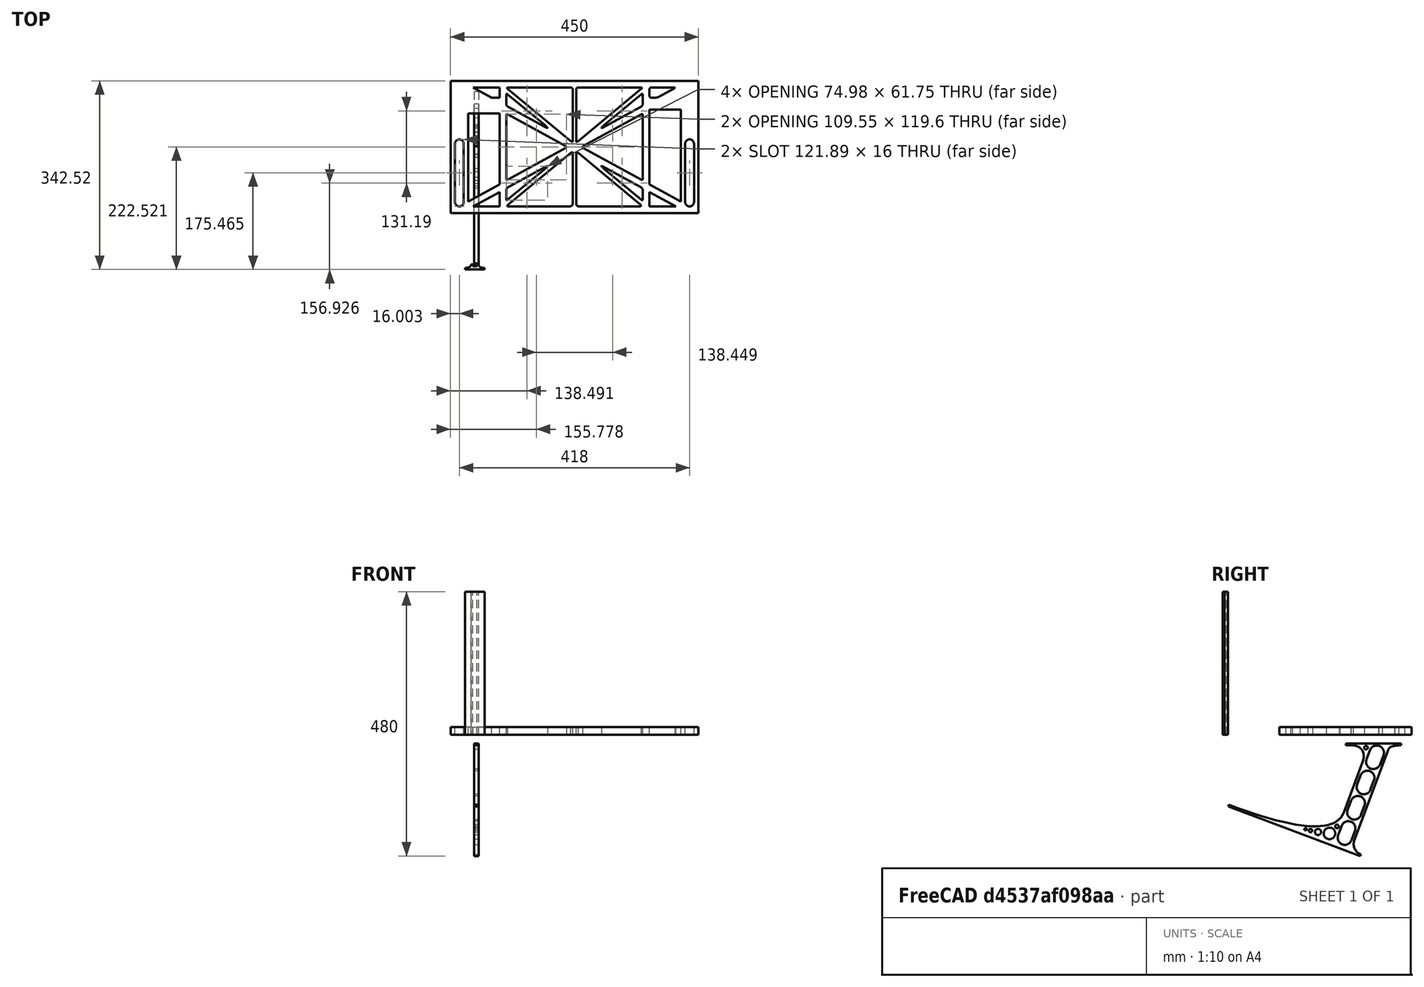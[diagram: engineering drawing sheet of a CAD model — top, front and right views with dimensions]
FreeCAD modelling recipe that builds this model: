
FCSTD DOCUMENT  (FreeCAD 0.19R0.19.2)
Label: laptopStand105
License: All rights reserved
LicenseURL: http://en.wikipedia.org/wiki/All_rights_reserved
objects: Sketcher::SketchObject×3, Part::Extrusion×3
note: 6 computed .brp shape members not serialized (recipe doc carries the construction recipe); baked Part::Feature solids carry a one-line shape summary decoded from their .brp

FEATURE [Sketcher::SketchObject] Sketch
  FullyConstrained = false
  sketch-geometry (288):
    g0: LineSegment StartX=-10.9272 StartY=-82.7794 StartZ=0 EndX=46.0728 EndY=-51.4823 EndZ=0
    g1: LineSegment StartX=366.073 StartY=-91.7794 StartZ=0 EndX=318.073 EndY=-65.424 EndZ=0
    g2: LineSegment StartX=-10.9272 StartY=77.3346 StartZ=0 EndX=-10.9272 EndY=-82.7794 EndZ=0
    g3: LineSegment StartX=-1.92719 StartY=-91.7794 StartZ=0 EndX=46.0728 EndY=-91.7794 EndZ=0
    g4: LineSegment StartX=318.073 StartY=-65.424 StartZ=0 EndX=318.073 EndY=-91.7794 EndZ=0
    g5: LineSegment StartX=318.073 StartY=-91.7794 StartZ=0 EndX=366.073 EndY=-91.7794 EndZ=0
    g6: LineSegment StartX=46.0728 StartY=-65.424 StartZ=0 EndX=-1.92719 EndY=-91.7794 EndZ=0
    g7: LineSegment StartX=46.0728 StartY=-65.424 StartZ=0 EndX=46.0728 EndY=-91.7794 EndZ=0
    g8: LineSegment StartX=46.0728 StartY=77.3346 StartZ=0 EndX=46.0728 EndY=-51.4823 EndZ=0
    g9: LineSegment StartX=-42.9272 StartY=136.221 StartZ=0 EndX=-42.9272 EndY=-103.779 EndZ=0
    g10: LineSegment StartX=407.073 StartY=136.221 StartZ=0 EndX=407.073 EndY=-103.779 EndZ=0
    g11: ArcOfCircle CenterX=-26.9272 CenterY=22.1087 CenterZ=0 NormalX=0 NormalY=0 NormalZ=1 AngleXU=0 Radius=8 StartAngle=1e-16 EndAngle=3.14159
    g12: ArcOfCircle CenterX=-26.9272 CenterY=-83.7794 CenterZ=0 NormalX=0 NormalY=0 NormalZ=1 AngleXU=0 Radius=8 StartAngle=3.14159 EndAngle=6.28319
    g13: LineSegment StartX=-34.9272 StartY=22.1087 StartZ=0 EndX=-34.9272 EndY=-83.7794 EndZ=0
    g14: LineSegment StartX=-18.9272 StartY=22.1087 StartZ=0 EndX=-18.9272 EndY=-83.7794 EndZ=0
    g15: ArcOfCircle CenterX=391.073 CenterY=22.1087 CenterZ=0 NormalX=0 NormalY=0 NormalZ=1 AngleXU=0 Radius=8 StartAngle=-4.4e-15 EndAngle=3.14159
    g16: LineSegment StartX=399.073 StartY=22.1087 StartZ=0 EndX=399.073 EndY=-83.7794 EndZ=0
    g17: LineSegment StartX=383.073 StartY=22.1087 StartZ=0 EndX=383.073 EndY=-83.7794 EndZ=0
    g18: ArcOfCircle CenterX=391.073 CenterY=-83.7794 CenterZ=0 NormalX=0 NormalY=0 NormalZ=1 AngleXU=0 Radius=8 StartAngle=3.14159 EndAngle=6.28319
    g19: Circle CenterX=175.022 CenterY=27.0628 CenterZ=0 NormalX=0 NormalY=0 NormalZ=1 AngleXU=0 Radius=1
    g20: Circle CenterX=179.022 CenterY=24.8665 CenterZ=0 NormalX=0 NormalY=0 NormalZ=1 AngleXU=0 Radius=1
    g21: Circle CenterX=179.022 CenterY=27.0628 CenterZ=0 NormalX=0 NormalY=0 NormalZ=1 AngleXU=0 Radius=1
    g22: BSplineCurve PolesCount=3 KnotsCount=2 Degree=2 IsPeriodic=0
    g23: GeomPoint X=175.022 Y=27.0628 Z=0
    g24: GeomPoint X=179.022 Y=27.0628 Z=0
    g25: Circle CenterX=189.124 CenterY=27.0628 CenterZ=0 NormalX=0 NormalY=0 NormalZ=1 AngleXU=0 Radius=1
    g26: Circle CenterX=185.124 CenterY=24.8665 CenterZ=0 NormalX=0 NormalY=0 NormalZ=1 AngleXU=0 Radius=1
    g27: Circle CenterX=185.124 CenterY=27.0628 CenterZ=0 NormalX=0 NormalY=0 NormalZ=1 AngleXU=0 Radius=1
    g28: BSplineCurve PolesCount=3 KnotsCount=2 Degree=2 IsPeriodic=0
    g29: GeomPoint X=189.124 Y=27.0628 Z=0
    g30: GeomPoint X=185.124 Y=27.0628 Z=0
    g31: Circle CenterX=175.022 CenterY=5.37834 CenterZ=0 NormalX=0 NormalY=0 NormalZ=1 AngleXU=0 Radius=1
    g32: Circle CenterX=179.022 CenterY=7.57463 CenterZ=0 NormalX=0 NormalY=0 NormalZ=1 AngleXU=0 Radius=1
    g33: Circle CenterX=179.022 CenterY=5.34704 CenterZ=0 NormalX=0 NormalY=0 NormalZ=1 AngleXU=0 Radius=1
    g34: BSplineCurve PolesCount=3 KnotsCount=2 Degree=2 IsPeriodic=0
    g35: GeomPoint X=175.022 Y=5.37834 Z=0
    g36: GeomPoint X=179.022 Y=5.34704 Z=0
    g37: Circle CenterX=189.124 CenterY=5.37834 CenterZ=0 NormalX=0 NormalY=0 NormalZ=1 AngleXU=0 Radius=1
    g38: Circle CenterX=185.124 CenterY=7.57463 CenterZ=0 NormalX=0 NormalY=0 NormalZ=1 AngleXU=0 Radius=1
    g39: Circle CenterX=185.124 CenterY=5.34704 CenterZ=0 NormalX=0 NormalY=0 NormalZ=1 AngleXU=0 Radius=1
    g40: BSplineCurve PolesCount=3 KnotsCount=2 Degree=2 IsPeriodic=0
    g41: GeomPoint X=189.124 Y=5.37834 Z=0
    g42: GeomPoint X=185.124 Y=5.34704 Z=0
    g43: Circle CenterX=165.871 CenterY=18.1458 CenterZ=0 NormalX=0 NormalY=0 NormalZ=1 AngleXU=0 Radius=1
    g44: Circle CenterX=169.377 CenterY=16.2206 CenterZ=0 NormalX=0 NormalY=0 NormalZ=1 AngleXU=0 Radius=1
    g45: Circle CenterX=165.871 CenterY=14.2954 CenterZ=0 NormalX=0 NormalY=0 NormalZ=1 AngleXU=0 Radius=1
    g46: BSplineCurve PolesCount=3 KnotsCount=2 Degree=2 IsPeriodic=0
    g47: GeomPoint X=165.871 Y=18.1458 Z=0
    g48: GeomPoint X=165.871 Y=14.2954 Z=0
    g49: Circle CenterX=198.275 CenterY=18.1458 CenterZ=0 NormalX=0 NormalY=0 NormalZ=1 AngleXU=0 Radius=1
    g50: Circle CenterX=194.768 CenterY=16.2206 CenterZ=0 NormalX=0 NormalY=0 NormalZ=1 AngleXU=0 Radius=1
    g51: Circle CenterX=198.275 CenterY=14.2954 CenterZ=0 NormalX=0 NormalY=0 NormalZ=1 AngleXU=0 Radius=1
    g52: BSplineCurve PolesCount=3 KnotsCount=2 Degree=2 IsPeriodic=0
    g53: GeomPoint X=198.275 Y=18.1458 Z=0
    g54: GeomPoint X=198.275 Y=14.2954 Z=0
    g55: LineSegment StartX=407.073 StartY=-103.779 StartZ=0 EndX=-42.9272 EndY=-103.779 EndZ=0
    g56: LineSegment StartX=407.073 StartY=136.221 StartZ=0 EndX=-42.9272 EndY=136.221 EndZ=0
    g57: LineSegment StartX=46.0728 StartY=77.3346 StartZ=0 EndX=-10.9272 EndY=77.3346 EndZ=0
    g58: LineSegment StartX=46.0728 StartY=105.865 StartZ=0 EndX=31.5028 EndY=105.865 EndZ=0
    g59: LineSegment StartX=46.0728 StartY=124.221 StartZ=0 EndX=46.0728 EndY=105.865 EndZ=0
    g60: LineSegment StartX=-1.92719 StartY=124.221 StartZ=0 EndX=31.5028 EndY=105.865 EndZ=0
    g61: LineSegment StartX=46.0728 StartY=124.221 StartZ=0 EndX=-1.92719 EndY=124.221 EndZ=0
    g62: Circle CenterX=125.607 CenterY=54.1951 CenterZ=0 NormalX=0 NormalY=0 NormalZ=1 AngleXU=0 Radius=1
    g63: Circle CenterX=139.632 CenterY=46.4944 CenterZ=0 NormalX=0 NormalY=0 NormalZ=1 AngleXU=0 Radius=1
    g64: Circle CenterX=127.326 CenterY=56.7187 CenterZ=0 NormalX=0 NormalY=0 NormalZ=1 AngleXU=0 Radius=1
    g65: BSplineCurve PolesCount=3 KnotsCount=2 Degree=2 IsPeriodic=0
    g66: GeomPoint X=125.607 Y=54.1951 Z=0
    g67: GeomPoint X=127.326 Y=56.7187 Z=0
    g68: Circle CenterX=236.821 CenterY=56.7187 CenterZ=0 NormalX=0 NormalY=0 NormalZ=1 AngleXU=0 Radius=1
    g69: Circle CenterX=224.513 CenterY=46.4944 CenterZ=0 NormalX=0 NormalY=0 NormalZ=1 AngleXU=0 Radius=1
    g70: Circle CenterX=238.538 CenterY=54.1951 CenterZ=0 NormalX=0 NormalY=0 NormalZ=1 AngleXU=0 Radius=1
    g71: BSplineCurve PolesCount=3 KnotsCount=2 Degree=2 IsPeriodic=0
    g72: GeomPoint X=236.821 Y=56.7187 Z=0
    g73: GeomPoint X=238.538 Y=54.1951 Z=0
    g74: Circle CenterX=238.538 CenterY=-21.7539 CenterZ=0 NormalX=0 NormalY=0 NormalZ=1 AngleXU=0 Radius=1
    g75: Circle CenterX=224.513 CenterY=-14.0532 CenterZ=0 NormalX=0 NormalY=0 NormalZ=1 AngleXU=0 Radius=1
    g76: Circle CenterX=236.821 CenterY=-24.2775 CenterZ=0 NormalX=0 NormalY=0 NormalZ=1 AngleXU=0 Radius=1
    g77: BSplineCurve PolesCount=3 KnotsCount=2 Degree=2 IsPeriodic=0
    g78: GeomPoint X=238.538 Y=-21.7539 Z=0
    g79: GeomPoint X=236.821 Y=-24.2775 Z=0
    g80: Circle CenterX=125.607 CenterY=-21.7539 CenterZ=0 NormalX=0 NormalY=0 NormalZ=1 AngleXU=0 Radius=1
    g81: Circle CenterX=139.632 CenterY=-14.0532 CenterZ=0 NormalX=0 NormalY=0 NormalZ=1 AngleXU=0 Radius=1
    g82: Circle CenterX=127.325 CenterY=-24.2775 CenterZ=0 NormalX=0 NormalY=0 NormalZ=1 AngleXU=0 Radius=1
    g83: BSplineCurve PolesCount=3 KnotsCount=2 Degree=2 IsPeriodic=0
    g84: GeomPoint X=125.607 Y=-21.7539 Z=0
    g85: GeomPoint X=127.325 Y=-24.2775 Z=0
    g86: Circle CenterX=302.996 CenterY=111.695 CenterZ=0 NormalX=0 NormalY=0 NormalZ=1 AngleXU=0 Radius=1
    g87: Circle CenterX=306.073 CenterY=114.251 CenterZ=0 NormalX=0 NormalY=0 NormalZ=1 AngleXU=0 Radius=1
    g88: Circle CenterX=306.073 CenterY=110.251 CenterZ=0 NormalX=0 NormalY=0 NormalZ=1 AngleXU=0 Radius=1
    g89: BSplineCurve PolesCount=3 KnotsCount=2 Degree=2 IsPeriodic=0
    g90: GeomPoint X=302.996 Y=111.695 Z=0
    g91: GeomPoint X=306.073 Y=110.251 Z=0
    g92: Circle CenterX=306.073 CenterY=95.2763 CenterZ=0 NormalX=0 NormalY=0 NormalZ=1 AngleXU=0 Radius=1
    g93: Circle CenterX=306.073 CenterY=91.2763 CenterZ=0 NormalX=0 NormalY=0 NormalZ=1 AngleXU=0 Radius=1
    g94: Circle CenterX=302.567 CenterY=89.3511 CenterZ=0 NormalX=0 NormalY=0 NormalZ=1 AngleXU=0 Radius=1
    g95: BSplineCurve PolesCount=3 KnotsCount=2 Degree=2 IsPeriodic=0
    g96: GeomPoint X=306.073 Y=95.2763 Z=0
    g97: GeomPoint X=302.567 Y=89.3511 Z=0
    g98: LineSegment StartX=306.073 StartY=110.251 StartZ=0 EndX=306.073 EndY=95.2763 EndZ=0
    g99: LineSegment StartX=302.996 StartY=111.695 StartZ=0 EndX=236.821 EndY=56.7187 EndZ=0
    g100: LineSegment StartX=238.538 StartY=54.1951 StartZ=0 EndX=302.567 EndY=89.3511 EndZ=0
    g101: Circle CenterX=61.1496 CenterY=111.695 CenterZ=0 NormalX=0 NormalY=0 NormalZ=1 AngleXU=0 Radius=1
    g102: Circle CenterX=58.0728 CenterY=114.251 CenterZ=0 NormalX=0 NormalY=0 NormalZ=1 AngleXU=0 Radius=1
    g103: Circle CenterX=58.0728 CenterY=110.251 CenterZ=0 NormalX=0 NormalY=0 NormalZ=1 AngleXU=0 Radius=1
    g104: BSplineCurve PolesCount=3 KnotsCount=2 Degree=2 IsPeriodic=0
    g105: GeomPoint X=61.1496 Y=111.695 Z=0
    g106: GeomPoint X=58.0728 Y=110.251 Z=0
    g107: Circle CenterX=61.5791 CenterY=89.3511 CenterZ=0 NormalX=0 NormalY=0 NormalZ=1 AngleXU=0 Radius=1
    g108: Circle CenterX=58.0728 CenterY=91.2763 CenterZ=0 NormalX=0 NormalY=0 NormalZ=1 AngleXU=0 Radius=1
    g109: Circle CenterX=58.0728 CenterY=95.2763 CenterZ=0 NormalX=0 NormalY=0 NormalZ=1 AngleXU=0 Radius=1
    g110: BSplineCurve PolesCount=3 KnotsCount=2 Degree=2 IsPeriodic=0
    g111: GeomPoint X=61.5791 Y=89.3511 Z=0
    g112: GeomPoint X=58.0728 Y=95.2763 Z=0
    g113: LineSegment StartX=58.0728 StartY=110.251 StartZ=0 EndX=58.0728 EndY=95.2763 EndZ=0
    g114: LineSegment StartX=61.1496 StartY=111.695 StartZ=0 EndX=127.326 EndY=56.7187 EndZ=0
    g115: LineSegment StartX=125.607 StartY=54.1951 StartZ=0 EndX=61.5791 EndY=89.3511 EndZ=0
    g116: Circle CenterX=61.5791 CenterY=-56.9099 CenterZ=0 NormalX=0 NormalY=0 NormalZ=1 AngleXU=0 Radius=1
    g117: Circle CenterX=58.0728 CenterY=-58.8351 CenterZ=0 NormalX=0 NormalY=0 NormalZ=1 AngleXU=0 Radius=1
    g118: Circle CenterX=58.0728 CenterY=-62.8351 CenterZ=0 NormalX=0 NormalY=0 NormalZ=1 AngleXU=0 Radius=1
    g119: BSplineCurve PolesCount=3 KnotsCount=2 Degree=2 IsPeriodic=0
    g120: GeomPoint X=61.5791 Y=-56.9099 Z=0
    g121: GeomPoint X=58.0728 Y=-62.8351 Z=0
    g122: Circle CenterX=58.0728 CenterY=-77.8102 CenterZ=0 NormalX=0 NormalY=0 NormalZ=1 AngleXU=0 Radius=1
    g123: Circle CenterX=58.0728 CenterY=-81.8102 CenterZ=0 NormalX=0 NormalY=0 NormalZ=1 AngleXU=0 Radius=1
    g124: Circle CenterX=61.1496 CenterY=-79.2541 CenterZ=0 NormalX=0 NormalY=0 NormalZ=1 AngleXU=0 Radius=1
    g125: BSplineCurve PolesCount=3 KnotsCount=2 Degree=2 IsPeriodic=0
    g126: GeomPoint X=58.0728 Y=-77.8102 Z=0
    g127: GeomPoint X=61.1496 Y=-79.2541 Z=0
    g128: LineSegment StartX=58.0728 StartY=-62.8351 StartZ=0 EndX=58.0728 EndY=-77.8102 EndZ=0
    g129: LineSegment StartX=61.1496 StartY=-79.2541 StartZ=0 EndX=127.325 EndY=-24.2775 EndZ=0
    g130: LineSegment StartX=125.607 StartY=-21.7539 StartZ=0 EndX=61.5791 EndY=-56.9099 EndZ=0
    g131: Circle CenterX=302.567 CenterY=-56.9099 CenterZ=0 NormalX=0 NormalY=0 NormalZ=1 AngleXU=0 Radius=1
    g132: Circle CenterX=306.073 CenterY=-58.8351 CenterZ=0 NormalX=0 NormalY=0 NormalZ=1 AngleXU=0 Radius=1
    g133: Circle CenterX=306.073 CenterY=-62.8351 CenterZ=0 NormalX=0 NormalY=0 NormalZ=1 AngleXU=0 Radius=1
    g134: BSplineCurve PolesCount=3 KnotsCount=2 Degree=2 IsPeriodic=0
    g135: GeomPoint X=302.567 Y=-56.9099 Z=0
    g136: GeomPoint X=306.073 Y=-62.8351 Z=0
    g137: Circle CenterX=302.996 CenterY=-79.2541 CenterZ=0 NormalX=0 NormalY=0 NormalZ=1 AngleXU=0 Radius=1
    g138: Circle CenterX=306.073 CenterY=-81.8102 CenterZ=0 NormalX=0 NormalY=0 NormalZ=1 AngleXU=0 Radius=1
    g139: Circle CenterX=306.073 CenterY=-77.8102 CenterZ=0 NormalX=0 NormalY=0 NormalZ=1 AngleXU=0 Radius=1
    g140: BSplineCurve PolesCount=3 KnotsCount=2 Degree=2 IsPeriodic=0
    g141: GeomPoint X=302.996 Y=-79.2541 Z=0
    g142: GeomPoint X=306.073 Y=-77.8102 Z=0
    g143: LineSegment StartX=306.073 StartY=-62.8351 StartZ=0 EndX=306.073 EndY=-77.8102 EndZ=0
    g144: LineSegment StartX=302.996 StartY=-79.2541 StartZ=0 EndX=236.821 EndY=-24.2775 EndZ=0
    g145: LineSegment StartX=238.538 StartY=-21.7539 StartZ=0 EndX=302.567 EndY=-56.9099 EndZ=0
    g146: Circle CenterX=61.6457 CenterY=-88.8112 CenterZ=0 NormalX=0 NormalY=0 NormalZ=1 AngleXU=0 Radius=1
    g147: Circle CenterX=58.0728 CenterY=-91.7794 CenterZ=0 NormalX=0 NormalY=0 NormalZ=1 AngleXU=0 Radius=1
    g148: Circle CenterX=63.9135 CenterY=-91.7794 CenterZ=0 NormalX=0 NormalY=0 NormalZ=1 AngleXU=0 Radius=1
    g149: BSplineCurve PolesCount=3 KnotsCount=2 Degree=2 IsPeriodic=0
    g150: GeomPoint X=61.6457 Y=-88.8112 Z=0
    g151: GeomPoint X=63.9135 Y=-91.7794 Z=0
    g152: Circle CenterX=179.022 CenterY=-85.8163 CenterZ=0 NormalX=0 NormalY=0 NormalZ=1 AngleXU=0 Radius=1
    g153: Circle CenterX=179.022 CenterY=-91.7794 CenterZ=0 NormalX=0 NormalY=0 NormalZ=1 AngleXU=0 Radius=1
    g154: Circle CenterX=171.895 CenterY=-91.7794 CenterZ=0 NormalX=0 NormalY=0 NormalZ=1 AngleXU=0 Radius=1
    g155: BSplineCurve PolesCount=3 KnotsCount=2 Degree=2 IsPeriodic=0
    g156: GeomPoint X=179.022 Y=-85.8163 Z=0
    g157: GeomPoint X=171.895 Y=-91.7794 Z=0
    g158: Circle CenterX=185.124 CenterY=-86.2028 CenterZ=0 NormalX=0 NormalY=0 NormalZ=1 AngleXU=0 Radius=1
    g159: Circle CenterX=185.124 CenterY=-91.7794 CenterZ=0 NormalX=0 NormalY=0 NormalZ=1 AngleXU=0 Radius=1
    g160: Circle CenterX=191.747 CenterY=-91.7794 CenterZ=0 NormalX=0 NormalY=0 NormalZ=1 AngleXU=0 Radius=1
    g161: BSplineCurve PolesCount=3 KnotsCount=2 Degree=2 IsPeriodic=0
    g162: GeomPoint X=185.124 Y=-86.2028 Z=0
    g163: GeomPoint X=191.747 Y=-91.7794 Z=0
    g164: Circle CenterX=299.888 CenterY=-86.6413 CenterZ=0 NormalX=0 NormalY=0 NormalZ=1 AngleXU=0 Radius=1
    g165: Circle CenterX=306.073 CenterY=-91.7794 CenterZ=0 NormalX=0 NormalY=0 NormalZ=1 AngleXU=0 Radius=1
    g166: Circle CenterX=298.776 CenterY=-91.7794 CenterZ=0 NormalX=0 NormalY=0 NormalZ=1 AngleXU=0 Radius=1
    g167: BSplineCurve PolesCount=3 KnotsCount=2 Degree=2 IsPeriodic=0
    g168: GeomPoint X=299.888 Y=-86.6413 Z=0
    g169: GeomPoint X=298.776 Y=-91.7794 Z=0
    g170: LineSegment StartX=189.124 StartY=5.37834 StartZ=0 EndX=299.888 EndY=-86.6413 EndZ=0
    g171: LineSegment StartX=298.776 StartY=-91.7794 StartZ=0 EndX=191.747 EndY=-91.7794 EndZ=0
    g172: LineSegment StartX=185.124 StartY=-86.2028 StartZ=0 EndX=185.124 EndY=5.34704 EndZ=0
    g173: LineSegment StartX=179.022 StartY=5.34704 StartZ=0 EndX=179.022 EndY=-85.8163 EndZ=0
    g174: LineSegment StartX=171.895 StartY=-91.7794 StartZ=0 EndX=63.9135 EndY=-91.7794 EndZ=0
    g175: LineSegment StartX=61.6457 StartY=-88.8112 StartZ=0 EndX=175.022 EndY=5.37834 EndZ=0
    g176: Circle CenterX=302.073 CenterY=124.221 CenterZ=0 NormalX=0 NormalY=0 NormalZ=1 AngleXU=0 Radius=1
    g177: Circle CenterX=306.073 CenterY=124.221 CenterZ=0 NormalX=0 NormalY=0 NormalZ=1 AngleXU=0 Radius=1
    g178: Circle CenterX=302.996 CenterY=121.665 CenterZ=0 NormalX=0 NormalY=0 NormalZ=1 AngleXU=0 Radius=1
    g179: BSplineCurve PolesCount=3 KnotsCount=2 Degree=2 IsPeriodic=0
    g180: GeomPoint X=302.073 Y=124.221 Z=0
    g181: GeomPoint X=302.996 Y=121.665 Z=0
    g182: Circle CenterX=189.124 CenterY=124.221 CenterZ=0 NormalX=0 NormalY=0 NormalZ=1 AngleXU=0 Radius=1
    g183: Circle CenterX=185.124 CenterY=124.221 CenterZ=0 NormalX=0 NormalY=0 NormalZ=1 AngleXU=0 Radius=1
    g184: Circle CenterX=185.124 CenterY=120.221 CenterZ=0 NormalX=0 NormalY=0 NormalZ=1 AngleXU=0 Radius=1
    g185: BSplineCurve PolesCount=3 KnotsCount=2 Degree=2 IsPeriodic=0
    g186: GeomPoint X=189.124 Y=124.221 Z=0
    g187: GeomPoint X=185.124 Y=120.221 Z=0
    g188: Circle CenterX=175.022 CenterY=124.221 CenterZ=0 NormalX=0 NormalY=0 NormalZ=1 AngleXU=0 Radius=1
    g189: Circle CenterX=179.022 CenterY=124.221 CenterZ=0 NormalX=0 NormalY=0 NormalZ=1 AngleXU=0 Radius=1
    g190: Circle CenterX=179.022 CenterY=120.221 CenterZ=0 NormalX=0 NormalY=0 NormalZ=1 AngleXU=0 Radius=1
    g191: BSplineCurve PolesCount=3 KnotsCount=2 Degree=2 IsPeriodic=0
    g192: GeomPoint X=175.022 Y=124.221 Z=0
    g193: GeomPoint X=179.022 Y=120.221 Z=0
    g194: Circle CenterX=62.0728 CenterY=124.221 CenterZ=0 NormalX=0 NormalY=0 NormalZ=1 AngleXU=0 Radius=1
    g195: Circle CenterX=58.0728 CenterY=124.221 CenterZ=0 NormalX=0 NormalY=0 NormalZ=1 AngleXU=0 Radius=1
    g196: Circle CenterX=61.1496 CenterY=121.665 CenterZ=0 NormalX=0 NormalY=0 NormalZ=1 AngleXU=0 Radius=1
    g197: BSplineCurve PolesCount=3 KnotsCount=2 Degree=2 IsPeriodic=0
    g198: GeomPoint X=62.0728 Y=124.221 Z=0
    g199: GeomPoint X=61.1496 Y=121.665 Z=0
    g200: LineSegment StartX=62.0728 StartY=124.221 StartZ=0 EndX=175.022 EndY=124.221 EndZ=0
    g201: LineSegment StartX=179.022 StartY=120.221 StartZ=0 EndX=179.022 EndY=27.0628 EndZ=0
    g202: LineSegment StartX=185.124 StartY=27.0628 StartZ=0 EndX=185.124 EndY=120.221 EndZ=0
    g203: LineSegment StartX=189.124 StartY=124.221 StartZ=0 EndX=302.073 EndY=124.221 EndZ=0
    g204: LineSegment StartX=302.996 StartY=121.665 StartZ=0 EndX=189.124 EndY=27.0628 EndZ=0
    g205: LineSegment StartX=175.022 StartY=27.0628 StartZ=0 EndX=61.1496 EndY=121.665 EndZ=0
    g206: Circle CenterX=61.5791 CenterY=75.4095 CenterZ=0 NormalX=0 NormalY=0 NormalZ=1 AngleXU=0 Radius=1
    g207: Circle CenterX=58.0728 CenterY=77.3346 CenterZ=0 NormalX=0 NormalY=0 NormalZ=1 AngleXU=0 Radius=1
    g208: Circle CenterX=58.0728 CenterY=73.3346 CenterZ=0 NormalX=0 NormalY=0 NormalZ=1 AngleXU=0 Radius=1
    g209: BSplineCurve PolesCount=3 KnotsCount=2 Degree=2 IsPeriodic=0
    g210: GeomPoint X=61.5791 Y=75.4095 Z=0
    g211: GeomPoint X=58.0728 Y=73.3346 Z=0
    g212: Circle CenterX=58.0728 CenterY=-40.8935 CenterZ=0 NormalX=0 NormalY=0 NormalZ=1 AngleXU=0 Radius=1
    g213: Circle CenterX=58.0728 CenterY=-44.8935 CenterZ=0 NormalX=0 NormalY=0 NormalZ=1 AngleXU=0 Radius=1
    g214: Circle CenterX=61.5791 CenterY=-42.9683 CenterZ=0 NormalX=0 NormalY=0 NormalZ=1 AngleXU=0 Radius=1
    g215: BSplineCurve PolesCount=3 KnotsCount=2 Degree=2 IsPeriodic=0
    g216: GeomPoint X=58.0728 Y=-40.8935 Z=0
    g217: GeomPoint X=61.5791 Y=-42.9683 Z=0
    g218: LineSegment StartX=61.5791 StartY=-42.9683 StartZ=0 EndX=165.871 EndY=14.2954 EndZ=0
    g219: LineSegment StartX=165.871 StartY=18.1458 StartZ=0 EndX=61.5791 EndY=75.4095 EndZ=0
    g220: LineSegment StartX=58.0728 StartY=73.3346 StartZ=0 EndX=58.0728 EndY=-40.8935 EndZ=0
    g221: Circle CenterX=302.567 CenterY=-42.9683 CenterZ=0 NormalX=0 NormalY=0 NormalZ=1 AngleXU=0 Radius=1
    g222: Circle CenterX=306.073 CenterY=-44.8935 CenterZ=0 NormalX=0 NormalY=0 NormalZ=1 AngleXU=0 Radius=1
    g223: Circle CenterX=306.073 CenterY=-40.8935 CenterZ=0 NormalX=0 NormalY=0 NormalZ=1 AngleXU=0 Radius=1
    g224: BSplineCurve PolesCount=3 KnotsCount=2 Degree=2 IsPeriodic=0
    g225: GeomPoint X=302.567 Y=-42.9683 Z=0
    g226: GeomPoint X=306.073 Y=-40.8935 Z=0
    g227: Circle CenterX=306.073 CenterY=73.3346 CenterZ=0 NormalX=0 NormalY=0 NormalZ=1 AngleXU=0 Radius=1
    g228: Circle CenterX=306.073 CenterY=77.3346 CenterZ=0 NormalX=0 NormalY=0 NormalZ=1 AngleXU=0 Radius=1
    g229: Circle CenterX=302.567 CenterY=75.4095 CenterZ=0 NormalX=0 NormalY=0 NormalZ=1 AngleXU=0 Radius=1
    g230: BSplineCurve PolesCount=3 KnotsCount=2 Degree=2 IsPeriodic=0
    g231: GeomPoint X=306.073 Y=73.3346 Z=0
    g232: GeomPoint X=302.567 Y=75.4095 Z=0
    g233: LineSegment StartX=302.567 StartY=-42.9683 StartZ=0 EndX=198.275 EndY=14.2954 EndZ=0
    g234: LineSegment StartX=198.275 StartY=18.1458 StartZ=0 EndX=302.567 EndY=75.4095 EndZ=0
    g235: LineSegment StartX=306.073 StartY=73.3346 StartZ=0 EndX=306.073 EndY=-40.8935 EndZ=0
    g236: LineSegment StartX=322.073 StartY=105.865 StartZ=0 EndX=328.643 EndY=105.865 EndZ=0
    g237: LineSegment StartX=318.073 StartY=120.221 StartZ=0 EndX=318.073 EndY=109.865 EndZ=0
    g238: LineSegment StartX=336.157 StartY=107.779 StartZ=0 EndX=362.567 EndY=122.294 EndZ=0
    g239: Circle CenterX=362.073 CenterY=124.221 CenterZ=0 NormalX=0 NormalY=0 NormalZ=1 AngleXU=0 Radius=1
    g240: Circle CenterX=366.073 CenterY=124.221 CenterZ=0 NormalX=0 NormalY=0 NormalZ=1 AngleXU=0 Radius=1
    g241: Circle CenterX=362.567 CenterY=122.294 CenterZ=0 NormalX=0 NormalY=0 NormalZ=1 AngleXU=0 Radius=1
    g242: BSplineCurve PolesCount=3 KnotsCount=2 Degree=2 IsPeriodic=0
    g243: GeomPoint X=362.073 Y=124.221 Z=0
    g244: GeomPoint X=362.567 Y=122.294 Z=0
    g245: Circle CenterX=322.073 CenterY=124.221 CenterZ=0 NormalX=0 NormalY=0 NormalZ=1 AngleXU=0 Radius=1
    g246: Circle CenterX=318.073 CenterY=124.221 CenterZ=0 NormalX=0 NormalY=0 NormalZ=1 AngleXU=0 Radius=1
    g247: Circle CenterX=318.073 CenterY=120.221 CenterZ=0 NormalX=0 NormalY=0 NormalZ=1 AngleXU=0 Radius=1
    g248: BSplineCurve PolesCount=3 KnotsCount=2 Degree=2 IsPeriodic=0
    g249: GeomPoint X=322.073 Y=124.221 Z=0
    g250: GeomPoint X=318.073 Y=120.221 Z=0
    g251: Circle CenterX=322.073 CenterY=105.865 CenterZ=0 NormalX=0 NormalY=0 NormalZ=1 AngleXU=0 Radius=1
    g252: Circle CenterX=318.073 CenterY=105.865 CenterZ=0 NormalX=0 NormalY=0 NormalZ=1 AngleXU=0 Radius=1
    g253: Circle CenterX=318.073 CenterY=109.865 CenterZ=0 NormalX=0 NormalY=0 NormalZ=1 AngleXU=0 Radius=1
    g254: BSplineCurve PolesCount=3 KnotsCount=2 Degree=2 IsPeriodic=0
    g255: GeomPoint X=322.073 Y=105.865 Z=0
    g256: GeomPoint X=318.073 Y=109.865 Z=0
    g257: Circle CenterX=336.157 CenterY=107.779 CenterZ=0 NormalX=0 NormalY=0 NormalZ=1 AngleXU=0 Radius=1
    g258: Circle CenterX=332.651 CenterY=105.853 CenterZ=0 NormalX=0 NormalY=0 NormalZ=1 AngleXU=0 Radius=1
    g259: Circle CenterX=328.643 CenterY=105.865 CenterZ=0 NormalX=0 NormalY=0 NormalZ=1 AngleXU=0 Radius=1
    g260: BSplineCurve PolesCount=3 KnotsCount=2 Degree=2 IsPeriodic=0
    g261: GeomPoint X=336.157 Y=107.779 Z=0
    g262: GeomPoint X=328.643 Y=105.865 Z=0
    g263: LineSegment StartX=322.073 StartY=124.221 StartZ=0 EndX=362.073 EndY=124.221 EndZ=0
    g264: Circle CenterX=371.567 CenterY=-80.8644 CenterZ=0 NormalX=0 NormalY=0 NormalZ=1 AngleXU=0 Radius=1
    g265: Circle CenterX=375.073 CenterY=-82.7896 CenterZ=0 NormalX=0 NormalY=0 NormalZ=1 AngleXU=0 Radius=1
    g266: Circle CenterX=375.073 CenterY=-78.7896 CenterZ=0 NormalX=0 NormalY=0 NormalZ=1 AngleXU=0 Radius=1
    g267: BSplineCurve PolesCount=3 KnotsCount=2 Degree=2 IsPeriodic=0
    g268: GeomPoint X=371.567 Y=-80.8644 Z=0
    g269: GeomPoint X=375.073 Y=-78.7896 Z=0
    g270: Circle CenterX=321.579 CenterY=-53.4075 CenterZ=0 NormalX=0 NormalY=0 NormalZ=1 AngleXU=0 Radius=1
    g271: Circle CenterX=318.073 CenterY=-51.4823 CenterZ=0 NormalX=0 NormalY=0 NormalZ=1 AngleXU=0 Radius=1
    g272: Circle CenterX=318.073 CenterY=-47.4823 CenterZ=0 NormalX=0 NormalY=0 NormalZ=1 AngleXU=0 Radius=1
    g273: BSplineCurve PolesCount=3 KnotsCount=2 Degree=2 IsPeriodic=0
    g274: GeomPoint X=321.579 Y=-53.4075 Z=0
    g275: GeomPoint X=318.073 Y=-47.4823 Z=0
    g276: Circle CenterX=318.073 CenterY=79.9235 CenterZ=0 NormalX=0 NormalY=0 NormalZ=1 AngleXU=0 Radius=1
    g277: Circle CenterX=318.073 CenterY=83.9235 CenterZ=0 NormalX=0 NormalY=0 NormalZ=1 AngleXU=0 Radius=1
    g278: Circle CenterX=322.073 CenterY=83.9235 CenterZ=0 NormalX=0 NormalY=0 NormalZ=1 AngleXU=0 Radius=1
    g279: BSplineCurve PolesCount=3 KnotsCount=2 Degree=2 IsPeriodic=0
    g280: GeomPoint X=318.073 Y=79.9235 Z=0
    g281: GeomPoint X=322.073 Y=83.9235 Z=0
    g282: Circle CenterX=375.073 CenterY=79.9235 CenterZ=0 NormalX=0 NormalY=0 NormalZ=1 AngleXU=0 Radius=1
    g283: Circle CenterX=375.073 CenterY=83.9235 CenterZ=0 NormalX=0 NormalY=0 NormalZ=1 AngleXU=0 Radius=1
    g284: Circle CenterX=371.073 CenterY=83.9235 CenterZ=0 NormalX=0 NormalY=0 NormalZ=1 AngleXU=0 Radius=1
    g285: BSplineCurve PolesCount=3 KnotsCount=2 Degree=2 IsPeriodic=0
    g286: GeomPoint X=375.073 Y=79.9235 Z=0
    g287: GeomPoint X=371.073 Y=83.9235 Z=0
  constraints (473):
    c: Horizontal(g3)
    c: Coincident(g4,g1)
    c: Coincident(g7,g6)
    c: Coincident(g0,g8)
    c: Block(g1)
    c: Block(g4)
    c: Block(g7)
    c: Block(g6)
    c: Block(g0)
    c: Block(g2)
    c: Block(g5)
    c: Block(g3)
    c: Vertical(g9)
    c: Vertical(g10)
    c: Block(g10)
    c: Block(g9)
    c: Tangent(g11,g14) = 1.5708
    c: Tangent(g11,g13) = -1.5708
    c: Tangent(g13,g12) = -1.5708
    c: Tangent(g14,g12) = 1.5708
    c: Vertical(g13)
    c: Equal(g11,g12)
    c: Block(g14)
    c: Block(g13)
    c: Tangent(g15,g16) = 1.5708
    c: Tangent(g16,g18) = 1.5708
    c: Equal(g15,g18)
    c: Coincident(g17,g15)
    c: Coincident(g17,g18)
    c: Block(g16)
    c: Block(g17)
    c: Weight(g19) = 1
    c: Equal(g19,g20)
    c: Equal(g19,g21)
    c: InternalAlignment(g19,g22)
    c: InternalAlignment(g20,g22)
    c: InternalAlignment(g21,g22)
    c: InternalAlignment(g23,g22)
    c: InternalAlignment(g24,g22)
    c: Weight(g25) = 1
    c: Equal(g25,g26)
    c: Equal(g25,g27)
    c: InternalAlignment(g25,g28)
    c: InternalAlignment(g26,g28)
    c: InternalAlignment(g27,g28)
    c: InternalAlignment(g29,g28)
    c: InternalAlignment(g30,g28)
    c: Block(g28)
    c: Block(g22)
    c: Weight(g31) = 1
    c: Equal(g31,g32)
    c: Equal(g31,g33)
    c: InternalAlignment(g31,g34)
    c: InternalAlignment(g32,g34)
    c: InternalAlignment(g33,g34)
    c: InternalAlignment(g35,g34)
    c: InternalAlignment(g36,g34)
    c: Weight(g37) = 1
    c: Equal(g37,g38)
    c: Equal(g37,g39)
    c: InternalAlignment(g37,g40)
    c: InternalAlignment(g38,g40)
    c: InternalAlignment(g39,g40)
    c: InternalAlignment(g41,g40)
    c: InternalAlignment(g42,g40)
    c: Block(g40)
    c: Block(g34)
    c: Weight(g43) = 1
    c: Equal(g43,g44)
    c: Equal(g43,g45)
    c: InternalAlignment(g43,g46)
    c: InternalAlignment(g44,g46)
    c: InternalAlignment(g45,g46)
    c: InternalAlignment(g47,g46)
    c: InternalAlignment(g48,g46)
    c: Weight(g49) = 1
    c: Equal(g49,g50)
    c: Equal(g49,g51)
    c: InternalAlignment(g49,g52)
    c: InternalAlignment(g50,g52)
    c: InternalAlignment(g51,g52)
    c: InternalAlignment(g53,g52)
    c: InternalAlignment(g54,g52)
    c: Block(g46)
    c: Block(g52)
    c: Coincident(g55,g10)
    c: Coincident(g55,g9)
    c: Horizontal(g55)
    c: Distance(g55) = 450
    c: Coincident(g56,g10)
    c: Coincident(g56,g9)
    c: Horizontal(g56)
    c: Horizontal(g57)
    c: Coincident(g8,g57)
    c: Horizontal(g58)
    c: Vertical(g59)
    c: Block(g59)
    c: Block(g58)
    c: Block(g57)
    c: Distance(g59) = 18.3554
    c: Coincident(g61,g59)
    c: Coincident(g61,g60)
    c: Horizontal(g61)
    c: Block(g61)
    c: Block(g60)
    c: Coincident(g58,g60)
    c: Coincident(g2,g57)
    c: Weight(g62) = 1
    c: Equal(g62,g63)
    c: Equal(g62,g64)
    c: InternalAlignment(g62,g65)
    c: InternalAlignment(g63,g65)
    c: InternalAlignment(g64,g65)
    c: InternalAlignment(g66,g65)
    c: InternalAlignment(g67,g65)
    c: Block(g65)
    c: Weight(g68) = 1
    c: Equal(g68,g69)
    c: Equal(g68,g70)
    c: InternalAlignment(g68,g71)
    c: InternalAlignment(g69,g71)
    c: InternalAlignment(g70,g71)
    c: InternalAlignment(g72,g71)
    c: InternalAlignment(g73,g71)
    c: Block(g71)
    c: Weight(g74) = 1
    c: Equal(g74,g75)
    c: Equal(g74,g76)
    c: InternalAlignment(g74,g77)
    c: InternalAlignment(g75,g77)
    c: InternalAlignment(g76,g77)
    c: InternalAlignment(g78,g77)
    c: InternalAlignment(g79,g77)
    c: Block(g77)
    c: Weight(g80) = 1
    c: Equal(g80,g81)
    c: Equal(g80,g82)
    c: InternalAlignment(g80,g83)
    c: InternalAlignment(g81,g83)
    c: InternalAlignment(g82,g83)
    c: InternalAlignment(g84,g83)
    c: InternalAlignment(g85,g83)
    c: Block(g83)
    c: Weight(g86) = 1
    c: Equal(g86,g87)
    c: Equal(g86,g88)
    c: InternalAlignment(g86,g89)
    c: InternalAlignment(g87,g89)
    c: InternalAlignment(g88,g89)
    c: InternalAlignment(g90,g89)
    c: InternalAlignment(g91,g89)
    c: Weight(g92) = 1
    c: Equal(g92,g93)
    c: Equal(g92,g94)
    c: InternalAlignment(g92,g95)
    c: InternalAlignment(g93,g95)
    c: InternalAlignment(g94,g95)
    c: InternalAlignment(g96,g95)
    c: InternalAlignment(g97,g95)
    c: Block(g89)
    c: Block(g95)
    c: Coincident(g98,g89)
    c: Coincident(g98,g95)
    c: Vertical(g98)
    c: Coincident(g99,g89)
    c: Coincident(g99,g71)
    c: Coincident(g100,g71)
    c: Coincident(g100,g95)
    c: Weight(g101) = 1
    c: Equal(g101,g102)
    c: Equal(g101,g103)
    c: InternalAlignment(g101,g104)
    c: InternalAlignment(g102,g104)
    c: InternalAlignment(g103,g104)
    c: InternalAlignment(g105,g104)
    c: InternalAlignment(g106,g104)
    c: Weight(g107) = 1
    c: Equal(g107,g108)
    c: Equal(g107,g109)
    c: InternalAlignment(g107,g110)
    c: InternalAlignment(g108,g110)
    c: InternalAlignment(g109,g110)
    c: InternalAlignment(g111,g110)
    c: InternalAlignment(g112,g110)
    c: Block(g104)
    c: Block(g110)
    c: Coincident(g113,g104)
    c: Coincident(g113,g110)
    c: Vertical(g113)
    c: Coincident(g114,g104)
    c: Coincident(g114,g65)
    c: Coincident(g115,g65)
    c: Coincident(g115,g110)
    c: Weight(g116) = 1
    c: Equal(g116,g117)
    c: Equal(g116,g118)
    c: InternalAlignment(g116,g119)
    c: InternalAlignment(g117,g119)
    c: InternalAlignment(g118,g119)
    c: InternalAlignment(g120,g119)
    c: InternalAlignment(g121,g119)
    c: Weight(g122) = 1
    c: Equal(g122,g123)
    c: Equal(g122,g124)
    c: InternalAlignment(g122,g125)
    c: InternalAlignment(g123,g125)
    c: InternalAlignment(g124,g125)
    c: InternalAlignment(g126,g125)
    c: InternalAlignment(g127,g125)
    c: Block(g119)
    c: Block(g125)
    c: Coincident(g128,g119)
    c: Coincident(g128,g125)
    c: Vertical(g128)
    c: Coincident(g129,g125)
    c: Coincident(g129,g83)
    c: Coincident(g130,g83)
    c: Coincident(g130,g119)
    c: Weight(g131) = 1
    c: Equal(g131,g132)
    c: Equal(g131,g133)
    c: InternalAlignment(g131,g134)
    c: InternalAlignment(g132,g134)
    c: InternalAlignment(g133,g134)
    c: InternalAlignment(g135,g134)
    c: InternalAlignment(g136,g134)
    c: Weight(g137) = 1
    c: Equal(g137,g138)
    c: Equal(g137,g139)
    c: InternalAlignment(g137,g140)
    c: InternalAlignment(g138,g140)
    c: InternalAlignment(g139,g140)
    c: InternalAlignment(g141,g140)
    c: InternalAlignment(g142,g140)
    c: Block(g134)
    c: Block(g140)
    c: Coincident(g143,g134)
    c: Coincident(g143,g140)
    c: Vertical(g143)
    c: Coincident(g144,g140)
    c: Coincident(g144,g77)
    c: Coincident(g145,g77)
    c: Coincident(g145,g134)
    c: Weight(g146) = 1
    c: Equal(g146,g147)
    c: Equal(g146,g148)
    c: InternalAlignment(g146,g149)
    c: InternalAlignment(g147,g149)
    c: InternalAlignment(g148,g149)
    c: InternalAlignment(g150,g149)
    c: InternalAlignment(g151,g149)
    c: Weight(g152) = 1
    c: Equal(g152,g153)
    c: Equal(g152,g154)
    c: InternalAlignment(g152,g155)
    c: InternalAlignment(g153,g155)
    c: InternalAlignment(g154,g155)
    c: InternalAlignment(g156,g155)
    c: InternalAlignment(g157,g155)
    c: Weight(g158) = 1
    c: Equal(g158,g159)
    c: Equal(g158,g160)
    c: InternalAlignment(g158,g161)
    c: InternalAlignment(g159,g161)
    c: InternalAlignment(g160,g161)
    c: InternalAlignment(g162,g161)
    c: InternalAlignment(g163,g161)
    c: Weight(g164) = 1
    c: Equal(g164,g165)
    c: Equal(g164,g166)
    c: InternalAlignment(g164,g167)
    c: InternalAlignment(g165,g167)
    c: InternalAlignment(g166,g167)
    c: InternalAlignment(g168,g167)
    c: InternalAlignment(g169,g167)
    c: Block(g167)
    c: Block(g161)
    c: Block(g155)
    c: Block(g149)
    c: Coincident(g170,g40)
    c: Coincident(g170,g167)
    c: Coincident(g171,g167)
    c: Coincident(g171,g161)
    c: Horizontal(g171)
    c: Coincident(g172,g161)
    c: Coincident(g172,g40)
    c: Vertical(g172)
    c: Coincident(g173,g34)
    c: Coincident(g173,g155)
    c: Vertical(g173)
    c: Coincident(g174,g155)
    c: Coincident(g174,g149)
    c: Horizontal(g174)
    c: Coincident(g175,g149)
    c: Coincident(g175,g34)
    c: Weight(g176) = 1
    c: Equal(g176,g177)
    c: Equal(g176,g178)
    c: InternalAlignment(g176,g179)
    c: InternalAlignment(g177,g179)
    c: InternalAlignment(g178,g179)
    c: InternalAlignment(g180,g179)
    c: InternalAlignment(g181,g179)
    c: Weight(g182) = 1
    c: Equal(g182,g183)
    c: Equal(g182,g184)
    c: InternalAlignment(g182,g185)
    c: InternalAlignment(g183,g185)
    c: InternalAlignment(g184,g185)
    c: InternalAlignment(g186,g185)
    c: InternalAlignment(g187,g185)
    c: Weight(g188) = 1
    c: Equal(g188,g189)
    c: Equal(g188,g190)
    c: InternalAlignment(g188,g191)
    c: InternalAlignment(g189,g191)
    c: InternalAlignment(g190,g191)
    c: InternalAlignment(g192,g191)
    c: InternalAlignment(g193,g191)
    c: Weight(g194) = 1
    c: Equal(g194,g195)
    c: Equal(g194,g196)
    c: InternalAlignment(g194,g197)
    c: InternalAlignment(g195,g197)
    c: InternalAlignment(g196,g197)
    c: InternalAlignment(g198,g197)
    c: InternalAlignment(g199,g197)
    c: Block(g197)
    c: Block(g191)
    c: Block(g185)
    c: Block(g179)
    c: Coincident(g200,g197)
    c: Coincident(g200,g191)
    c: Horizontal(g200)
    c: Coincident(g201,g191)
    c: Coincident(g201,g22)
    c: Vertical(g201)
    c: Coincident(g202,g28)
    c: Coincident(g202,g185)
    c: Vertical(g202)
    c: Coincident(g203,g185)
    c: Coincident(g203,g179)
    c: Horizontal(g203)
    c: Coincident(g204,g179)
    c: Coincident(g204,g28)
    c: Coincident(g205,g22)
    c: Weight(g206) = 1
    c: Equal(g206,g207)
    c: Equal(g206,g208)
    c: InternalAlignment(g206,g209)
    c: InternalAlignment(g207,g209)
    c: InternalAlignment(g208,g209)
    c: InternalAlignment(g210,g209)
    c: InternalAlignment(g211,g209)
    c: Weight(g212) = 1
    c: Equal(g212,g213)
    c: Equal(g212,g214)
    c: InternalAlignment(g212,g215)
    c: InternalAlignment(g213,g215)
    c: InternalAlignment(g214,g215)
    c: InternalAlignment(g216,g215)
    c: InternalAlignment(g217,g215)
    c: Block(g215)
    c: Block(g209)
    c: Coincident(g218,g215)
    c: Coincident(g218,g46)
    c: Coincident(g219,g46)
    c: Coincident(g219,g209)
    c: Coincident(g220,g209)
    c: Coincident(g220,g215)
    c: Vertical(g220)
    c: Weight(g221) = 1
    c: Equal(g221,g222)
    c: Equal(g221,g223)
    c: InternalAlignment(g221,g224)
    c: InternalAlignment(g222,g224)
    c: InternalAlignment(g223,g224)
    c: InternalAlignment(g225,g224)
    c: InternalAlignment(g226,g224)
    c: Weight(g227) = 1
    c: Equal(g227,g228)
    c: Equal(g227,g229)
    c: InternalAlignment(g227,g230)
    c: InternalAlignment(g228,g230)
    c: InternalAlignment(g229,g230)
    c: InternalAlignment(g231,g230)
    c: InternalAlignment(g232,g230)
    c: Block(g230)
    c: Block(g224)
    c: Coincident(g233,g224)
    c: Coincident(g233,g52)
    c: Coincident(g234,g52)
    c: Coincident(g234,g230)
    c: Coincident(g235,g230)
    c: Coincident(g235,g224)
    c: Vertical(g235)
    c: Horizontal(g236)
    c: Block(g236)
    c: Vertical(g237)
    c: Block(g237)
    c: Block(g238)
    c: Weight(g239) = 1
    c: Equal(g239,g240)
    c: Equal(g239,g241)
    c: InternalAlignment(g239,g242)
    c: InternalAlignment(g240,g242)
    c: InternalAlignment(g241,g242)
    c: InternalAlignment(g243,g242)
    c: InternalAlignment(g244,g242)
    c: Weight(g245) = 1
    c: Equal(g245,g246)
    c: Equal(g245,g247)
    c: InternalAlignment(g245,g248)
    c: InternalAlignment(g246,g248)
    c: InternalAlignment(g247,g248)
    c: InternalAlignment(g249,g248)
    c: InternalAlignment(g250,g248)
    c: Weight(g251) = 1
    c: Equal(g251,g252)
    c: Equal(g251,g253)
    c: InternalAlignment(g251,g254)
    c: InternalAlignment(g252,g254)
    c: InternalAlignment(g253,g254)
    c: InternalAlignment(g255,g254)
    c: InternalAlignment(g256,g254)
    c: Weight(g257) = 1
    c: Equal(g257,g258)
    c: Equal(g257,g259)
    c: InternalAlignment(g257,g260)
    c: InternalAlignment(g258,g260)
    c: InternalAlignment(g259,g260)
    c: InternalAlignment(g261,g260)
    c: InternalAlignment(g262,g260)
    c: Block(g242)
    c: Block(g248)
    c: Block(g254)
    c: Block(g260)
    c: Coincident(g263,g248)
    c: Coincident(g263,g242)
    c: Horizontal(g263)
    c: Block(g205)
    c: Weight(g264) = 1
    c: Equal(g264,g265)
    c: Equal(g264,g266)
    c: InternalAlignment(g264,g267)
    c: InternalAlignment(g265,g267)
    c: InternalAlignment(g266,g267)
    c: InternalAlignment(g268,g267)
    c: InternalAlignment(g269,g267)
    c: Weight(g270) = 1
    c: Equal(g270,g271)
    c: Equal(g270,g272)
    c: InternalAlignment(g270,g273)
    c: InternalAlignment(g271,g273)
    c: InternalAlignment(g272,g273)
    c: InternalAlignment(g274,g273)
    c: InternalAlignment(g275,g273)
    c: Weight(g276) = 1
    c: Equal(g276,g277)
    c: Equal(g276,g278)
    c: InternalAlignment(g276,g279)
    c: InternalAlignment(g277,g279)
    c: InternalAlignment(g278,g279)
    c: InternalAlignment(g280,g279)
    c: InternalAlignment(g281,g279)
    c: Weight(g282) = 1
    c: Equal(g282,g283)
    c: Equal(g282,g284)
    c: InternalAlignment(g282,g285)
    c: InternalAlignment(g283,g285)
    c: InternalAlignment(g284,g285)
    c: InternalAlignment(g286,g285)
    c: InternalAlignment(g287,g285)
FEATURE [Sketcher::SketchObject] Sketch001
  FullyConstrained = true
  MapMode = 4
  Placement = pos=(0,0,0) rot=(0.57735,0.57735,0.57735;2.0944rad)
  Support = -> [Sketch]
  sketch-geometry (46):
    g0: BSplineCurve PolesCount=3 KnotsCount=2 Degree=2 IsPeriodic=0
    g1: ArcOfCircle CenterX=73.1223 CenterY=-32.291 CenterZ=0 NormalX=0 NormalY=0 NormalZ=1 AngleXU=0 Radius=13 StartAngle=5.92268 EndAngle=9.06428
    g2: ArcOfCircle CenterX=66.7816 CenterY=-49.1439 CenterZ=0 NormalX=0 NormalY=0 NormalZ=1 AngleXU=0 Radius=13 StartAngle=2.78068 EndAngle=5.92131
    g3: ArcOfCircle CenterX=55.9263 CenterY=-78.1807 CenterZ=0 NormalX=0 NormalY=0 NormalZ=1 AngleXU=0 Radius=13 StartAngle=5.92268 EndAngle=9.06428
    g4: ArcOfCircle CenterX=49.5884 CenterY=-95.0342 CenterZ=0 NormalX=0 NormalY=0 NormalZ=1 AngleXU=0 Radius=13 StartAngle=2.78068 EndAngle=5.92131
    g5: ArcOfCircle CenterX=38.7206 CenterY=-124.067 CenterZ=0 NormalX=0 NormalY=0 NormalZ=1 AngleXU=0 Radius=13 StartAngle=5.92268 EndAngle=9.06428
    g6: ArcOfCircle CenterX=32.3875 CenterY=-140.92 CenterZ=0 NormalX=0 NormalY=0 NormalZ=1 AngleXU=0 Radius=13 StartAngle=2.78068 EndAngle=5.92131
    g7: ArcOfCircle CenterX=21.4715 CenterY=-169.934 CenterZ=0 NormalX=0 NormalY=0 NormalZ=1 AngleXU=0 Radius=13 StartAngle=5.92268 EndAngle=9.06428
    g8: ArcOfCircle CenterX=15.1336 CenterY=-186.787 CenterZ=0 NormalX=0 NormalY=0 NormalZ=1 AngleXU=0 Radius=13 StartAngle=2.78068 EndAngle=5.92131
    g9-g12: Circle x4 (B-spline internal-alignment scaffolding for g13; pole/knot coordinates omitted)
    g13: BSplineCurve PolesCount=4 KnotsCount=2 Degree=3 IsPeriodic=0
    g14: GeomPoint X=28.8094 Y=-19.0875 Z=0
    g15: GeomPoint X=47.0443 Y=-50.4712 Z=0
    g16: Circle CenterX=53.5586 CenterY=-23.2695 CenterZ=0 NormalX=0 NormalY=0 NormalZ=1 AngleXU=0 Radius=3.24518
    g17: Circle CenterX=-195.441 CenterY=-127.082 CenterZ=0 NormalX=0 NormalY=0 NormalZ=1 AngleXU=0 Radius=1
    g18: Circle CenterX=-8.24091 CenterY=-197.481 CenterZ=0 NormalX=0 NormalY=0 NormalZ=1 AngleXU=0 Radius=1
    g19: Circle CenterX=12.8789 CenterY=-141.321 CenterZ=0 NormalX=0 NormalY=0 NormalZ=1 AngleXU=0 Radius=1
    g20: BSplineCurve PolesCount=3 KnotsCount=2 Degree=2 IsPeriodic=0
    g21: GeomPoint X=-195.441 Y=-127.082 Z=0
    g22: GeomPoint X=12.8789 Y=-141.321 Z=0
    g23: Circle CenterX=-12.8016 CenterY=-179.036 CenterZ=0 NormalX=0 NormalY=0 NormalZ=1 AngleXU=0 Radius=10.5072
    g24: Circle CenterX=0.933922 CenterY=-166.43 CenterZ=0 NormalX=0 NormalY=0 NormalZ=1 AngleXU=0 Radius=3.26661
    g25: Circle CenterX=-33.5518 CenterY=-176.44 CenterZ=0 NormalX=0 NormalY=0 NormalZ=1 AngleXU=0 Radius=5.64388
    g26: Circle CenterX=-47.2366 CenterY=-173.859 CenterZ=0 NormalX=0 NormalY=0 NormalZ=1 AngleXU=0 Radius=3.01653
    g27: Circle CenterX=-56.2595 CenterY=-171.456 CenterZ=0 NormalX=0 NormalY=0 NormalZ=1 AngleXU=0 Radius=2.12826
    g28: ArcOfCircle CenterX=51.2151 CenterY=-198.473 CenterZ=0 NormalX=0 NormalY=0 NormalZ=1 AngleXU=0 Radius=20 StartAngle=2.78189 EndAngle=4.35269
    g29: LineSegment StartX=32.4951 StartY=-191.433 StartZ=0 EndX=94.6578 EndY=-26.1352 EndZ=0
    g30: LineSegment StartX=43.1192 StartY=-220.001 StartZ=0 EndX=-196.497 EndY=-129.89 EndZ=0
    g31: LineSegment StartX=43.1192 StartY=-220.001 StartZ=0 EndX=44.1752 EndY=-217.193 EndZ=0
    g32: LineSegment StartX=117.223 StartY=-19.0875 StartZ=0 EndX=117.223 EndY=-16.0875 EndZ=0
    g33: LineSegment StartX=117.223 StartY=-16.0875 StartZ=0 EndX=17.2232 EndY=-16.0875 EndZ=0
    g34: LineSegment StartX=17.2232 StartY=-16.0875 StartZ=0 EndX=17.2232 EndY=-19.0875 EndZ=0
    g35: LineSegment StartX=28.8094 StartY=-19.0875 StartZ=0 EndX=17.2232 EndY=-19.0875 EndZ=0
    g36: LineSegment StartX=47.0443 StartY=-50.4712 StartZ=0 EndX=12.8789 EndY=-141.321 EndZ=0
    g37: LineSegment StartX=-195.441 StartY=-127.082 StartZ=0 EndX=-196.497 EndY=-129.89 EndZ=0
    g38: LineSegment StartX=85.2866 StartY=-36.8766 StartZ=0 EndX=78.9396 EndY=-53.7463 EndZ=0
    g39: LineSegment StartX=60.9579 StartY=-27.7053 StartZ=0 EndX=54.6191 EndY=-44.5532 EndZ=0
    g40: LineSegment StartX=68.0907 StartY=-82.7664 StartZ=0 EndX=61.7465 EndY=-99.6365 EndZ=0
    g41: LineSegment StartX=43.7619 StartY=-73.595 StartZ=0 EndX=37.426 EndY=-90.4435 EndZ=0
    g42: LineSegment StartX=50.885 StartY=-128.652 StartZ=0 EndX=44.5456 EndY=-145.522 EndZ=0
    g43: LineSegment StartX=26.5562 StartY=-119.481 StartZ=0 EndX=20.2251 EndY=-136.329 EndZ=0
    g44: LineSegment StartX=9.3071 StartY=-165.349 StartZ=0 EndX=2.97115 EndY=-182.197 EndZ=0
    g45: LineSegment StartX=33.6358 StartY=-174.52 StartZ=0 EndX=27.2917 EndY=-191.39 EndZ=0
  constraints (71):
    c: Block(g0)
    c: Block(g1)
    c: Block(g2)
    c: Block(g4)
    c: Block(g3)
    c: Block(g6)
    c: Block(g5)
    c: Block(g8)
    c: Block(g7)
    c: Weight(g9) = 1
    c: Equal(g9,g10)
    c: Equal(g9,g11)
    c: Equal(g9,g12)
    c: InternalAlignment(g9-g12 -> g13) x4
    c: InternalAlignment(g14,g13)
    c: InternalAlignment(g15,g13)
    c: Block(g16)
    c: Weight(g17) = 1
    c: Equal(g17,g18)
    c: Equal(g17,g19)
    c: InternalAlignment(g17,g20)
    c: InternalAlignment(g18,g20)
    c: InternalAlignment(g19,g20)
    c: InternalAlignment(g21,g20)
    c: InternalAlignment(g22,g20)
    c: Block(g20)
    c: Block(g23)
    c: Block(g24)
    c: Block(g25)
    c: Block(g26)
    c: Block(g27)
    c: Block(g28)
    c: Coincident(g29,g28)
    c: Coincident(g29,g0)
    c: Block(g13)
    c: Coincident(g31,g30)
    c: Coincident(g31,g28)
    c: Block(g31)
    c: Coincident(g32,g0)
    c: Vertical(g32)
    c: Coincident(g33,g32)
    c: Horizontal(g33)
    c: Coincident(g34,g33)
    c: Vertical(g34)
    c: Block(g33)
    c: Coincident(g35,g13)
    c: Coincident(g35,g34)
    c: Horizontal(g35)
    c: Coincident(g36,g13)
    c: Coincident(g36,g20)
    c: Coincident(g37,g20)
    c: Coincident(g37,g30)
    c: Block(g30)
    c: Coincident(g38,g1)
    c: Coincident(g38,g2)
    c: Coincident(g39,g1)
    c: Coincident(g39,g2)
    c: Coincident(g40,g3)
    c: Coincident(g40,g4)
    c: Coincident(g41,g3)
    c: Coincident(g41,g4)
    c: Coincident(g42,g5)
    c: Coincident(g42,g6)
    c: Coincident(g43,g5)
    c: Coincident(g43,g6)
    c: Coincident(g44,g7)
    c: Coincident(g44,g8)
    c: Coincident(g45,g7)
    c: Coincident(g45,g8)
    c: Distance(g30) = 256
    c: Distance(g33) = 100
FEATURE [Part::Extrusion] Extrude002
  Base = -> Sketch001
  Dir = (1,0,0)
  DirMode = 2
  FaceMakerClass = Part::FaceMakerBullseye
  LengthFwd = 8
  LengthRev = 0
  Solid = true
  Symmetric = false
FEATURE [Sketcher::SketchObject] Sketch002
  FullyConstrained = true
  sketch-geometry (20):
    g0: LineSegment StartX=-2.77179 StartY=-200.304 StartZ=0 EndX=5.22821 EndY=-200.304 EndZ=0
    g1: LineSegment StartX=5.22821 StartY=-200.304 StartZ=0 EndX=5.22821 EndY=-197.304 EndZ=0
    g2: LineSegment StartX=-2.77179 StartY=-200.304 StartZ=0 EndX=-2.77179 EndY=-197.304 EndZ=0
    g3: LineSegment StartX=5.22821 StartY=-197.304 StartZ=0 EndX=8.22821 EndY=-197.304 EndZ=0
    g4: LineSegment StartX=-2.77179 StartY=-197.304 StartZ=0 EndX=-5.77179 EndY=-197.304 EndZ=0
    g5: LineSegment StartX=19.2282 StartY=-203.304 StartZ=0 EndX=19.2282 EndY=-206.304 EndZ=0
    g6: LineSegment StartX=-16.7718 StartY=-203.304 StartZ=0 EndX=-16.7718 EndY=-206.304 EndZ=0
    g7: LineSegment StartX=-16.7718 StartY=-206.304 StartZ=0 EndX=19.2282 EndY=-206.304 EndZ=0
    g8: Circle CenterX=-16.7718 CenterY=-203.304 CenterZ=0 NormalX=0 NormalY=0 NormalZ=1 AngleXU=0 Radius=1
    g9: Circle CenterX=-5.77179 CenterY=-203.304 CenterZ=0 NormalX=0 NormalY=0 NormalZ=1 AngleXU=0 Radius=1
    g10: Circle CenterX=-5.77179 CenterY=-197.304 CenterZ=0 NormalX=0 NormalY=0 NormalZ=1 AngleXU=0 Radius=1
    g11: BSplineCurve PolesCount=3 KnotsCount=2 Degree=2 IsPeriodic=0
    g12: GeomPoint X=-16.7718 Y=-203.304 Z=0
    g13: GeomPoint X=-5.77179 Y=-197.304 Z=0
    g14: Circle CenterX=19.2282 CenterY=-203.304 CenterZ=0 NormalX=0 NormalY=0 NormalZ=1 AngleXU=0 Radius=1
    g15: Circle CenterX=8.22821 CenterY=-203.304 CenterZ=0 NormalX=0 NormalY=0 NormalZ=1 AngleXU=0 Radius=1
    g16: Circle CenterX=8.22821 CenterY=-197.304 CenterZ=0 NormalX=0 NormalY=0 NormalZ=1 AngleXU=0 Radius=1
    g17: BSplineCurve PolesCount=3 KnotsCount=2 Degree=2 IsPeriodic=0
    g18: GeomPoint X=19.2282 Y=-203.304 Z=0
    g19: GeomPoint X=8.22821 Y=-197.304 Z=0
  constraints (41):
    c: Horizontal(g0)
    c: Distance(g0) = 8
    c: Coincident(g1,g0)
    c: Vertical(g1)
    c: Distance(g1) = 3
    c: Coincident(g2,g0)
    c: Vertical(g2)
    c: Distance(g2) = 3
    c: Coincident(g3,g1)
    c: Horizontal(g3)
    c: Distance(g3) = 3
    c: Coincident(g4,g2)
    c: Horizontal(g4)
    c: Distance(g4) = 3
    c: Vertical(g5)
    c: Vertical(g6)
    c: Coincident(g7,g6)
    c: Coincident(g7,g5)
    c: Weight(g8) = 1
    c: Equal(g8,g9)
    c: Equal(g8,g10)
    c: Coincident(g11,g4)
    c: InternalAlignment(g8,g11)
    c: InternalAlignment(g9,g11)
    c: InternalAlignment(g10,g11)
    c: InternalAlignment(g12,g11)
    c: InternalAlignment(g13,g11)
    c: Coincident(g17,g5)
    c: Weight(g14) = 1
    c: Equal(g14,g15)
    c: Equal(g14,g16)
    c: Coincident(g17,g3)
    c: InternalAlignment(g14,g17)
    c: InternalAlignment(g15,g17)
    c: InternalAlignment(g16,g17)
    c: InternalAlignment(g18,g17)
    c: InternalAlignment(g19,g17)
    c: Block(g7)
    c: Block(g17)
    c: Block(g11)
    c: Block(g6)
FEATURE [Part::Extrusion] Extrude003
  Base = -> Sketch002
  Dir = (0,0,1)
  DirMode = 2
  FaceMakerClass = Part::FaceMakerBullseye
  LengthFwd = 260
  LengthRev = 0
  Solid = true
  Symmetric = false
FEATURE [Part::Extrusion] Extrude
  Base = -> Sketch
  Dir = (0,0,1)
  DirMode = 2
  FaceMakerClass = Part::FaceMakerBullseye
  LengthFwd = 14
  LengthRev = 0
  Solid = true
  Symmetric = false
